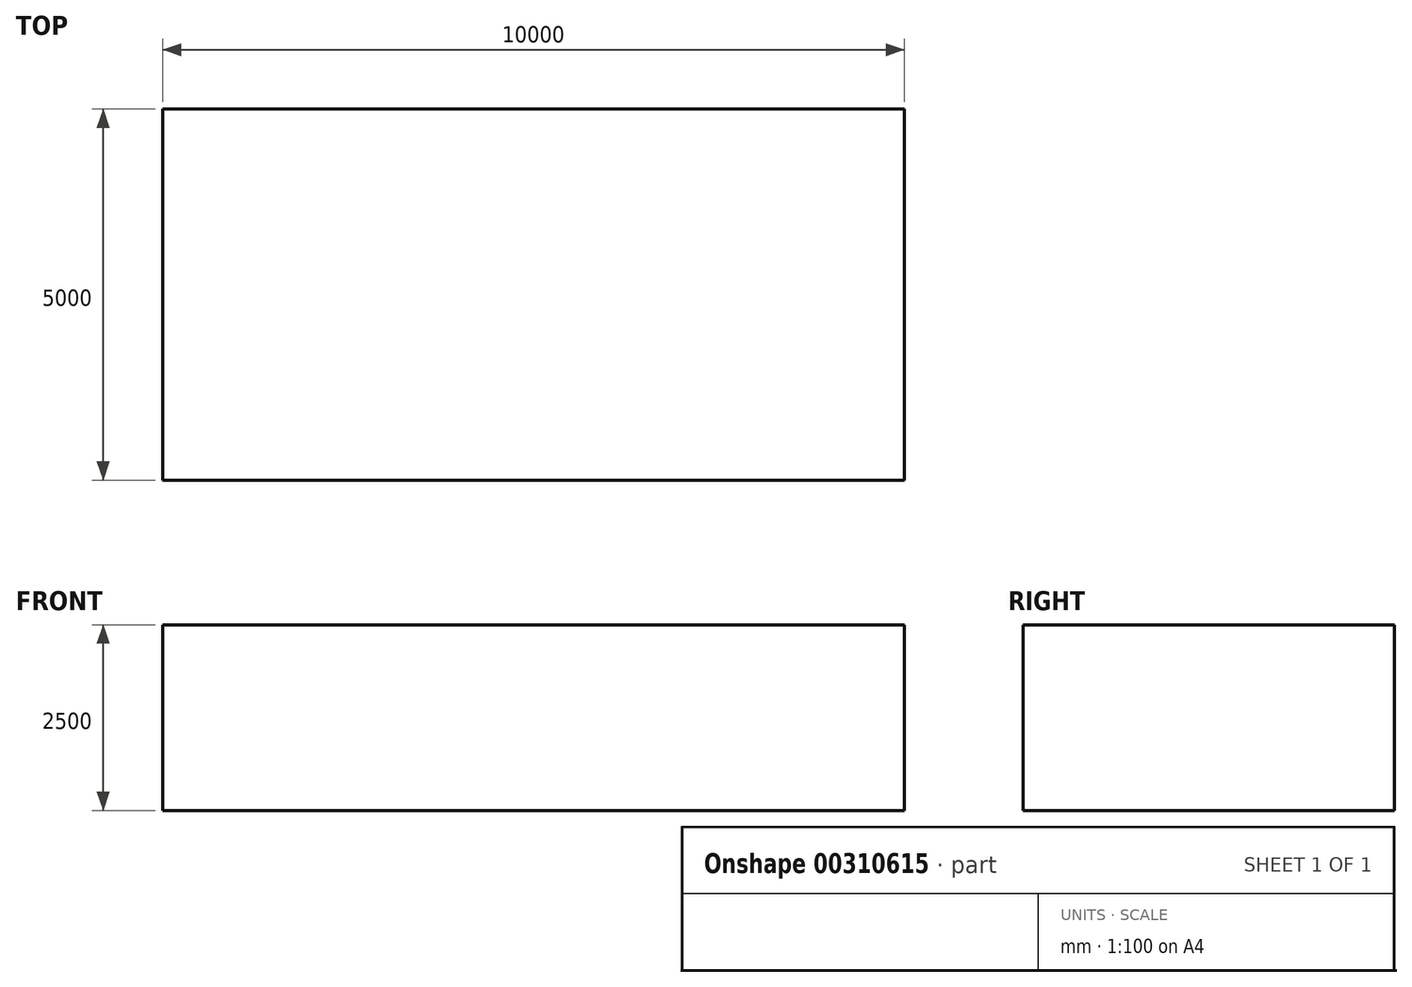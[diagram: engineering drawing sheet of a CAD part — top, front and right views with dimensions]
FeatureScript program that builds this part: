
annotation { "Feature Type Name" : "Feature", "Feature Type Description" : "" }
export const myFeature = defineFeature(function(context is Context, id is Id, definition is map)
    precondition{}
    {
        {
            var Q0;
            Q0=qCreatedBy(makeId("Front.planeOp"),FACE);
            var sketch = newSketch(context, id + "F0", { "sketchPlane" : qUnion([Q0])});
            skLineSegment(sketch, "E0.bottom", {"start": v(5000, 1250) * mm, "end": v(-5000, 1250) * mm});
            skLineSegment(sketch, "E0.top", {"start": v(5000, -1250) * mm, "end": v(-5000, -1250) * mm});
            skLineSegment(sketch, "E0.left", {"start": v(5000, 1250) * mm, "end": v(5000, -1250) * mm});
            skLineSegment(sketch, "E0.right", {"start": v(-5000, 1250) * mm, "end": v(-5000, -1250) * mm});
            skPoint(sketch, "E0.middle", {"position": v(0, 0) * mm});
            skSolve(sketch);
        }
        {
            var Q0;
            Q0=makeQuery(id+"F0.imprint","IMPRINT",FACE,{"disambiguationData":[TD([[makeQuery(id+"F0.imprint","IMPRINT",EDGE,{"derivedFrom":sQuery(id+"F0.wireOp",EDGE,"E0.bottom")}),1.0]])]});
            extrude(context, id + "F1", {"entities" : qUnion([Q0]), "depth" : 5000 * mm});
        }
    });
